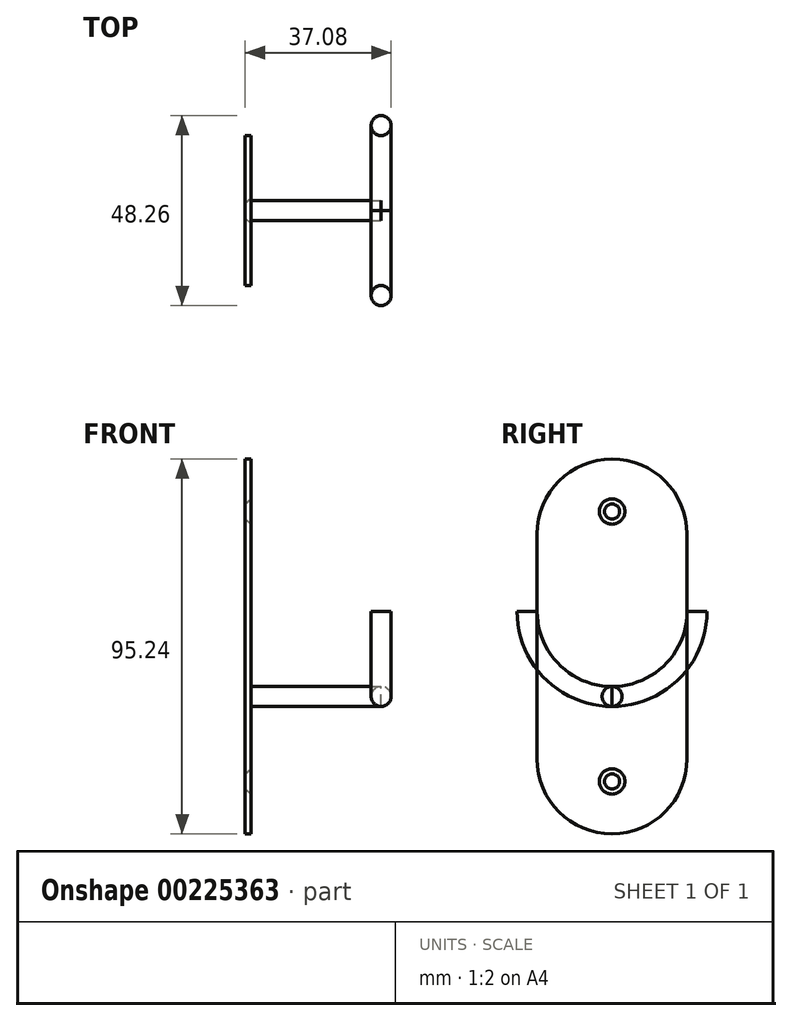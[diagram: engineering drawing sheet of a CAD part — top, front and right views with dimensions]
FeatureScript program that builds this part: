
annotation { "Feature Type Name" : "Feature", "Feature Type Description" : "" }
export const myFeature = defineFeature(function(context is Context, id is Id, definition is map)
    precondition{}
    {
        {
            var Q0;
            Q0=qCreatedBy(makeId("Right.planeOp"),FACE);
            var sketch = newSketch(context, id + "F0", { "sketchPlane" : qUnion([Q0])});
            skCircle(sketch, "E0", {"center": v(0, 0) * mm, "radius": 19.05 * mm, "construction": true});
            skLineSegment(sketch, "E1", {"start": v(-19.05, 0) * mm, "end": v(-19.05, 28.58) * mm});
            skArc(sketch, "E2", {"start": v(0, 47.63) * mm, "mid": v(-13.47, 42.05) * mm, "end": v(-19.05, 28.58) * mm});
            skLineSegment(sketch, "E3", {"start": v(0, 47.62) * mm, "end": v(0, 0) * mm, "construction": true});
            skArc(sketch, "E4.MirrorCS", {"start": v(0, 47.63) * mm, "mid": v(13.47, 42.05) * mm, "end": v(19.05, 28.58) * mm});
            skLineSegment(sketch, "E5.MirrorCS", {"start": v(19.05, 0) * mm, "end": v(19.05, 28.58) * mm});
            skLineSegment(sketch, "E6.MirrorCS", {"start": v(19.05, 0) * mm, "end": v(19.05, -28.58) * mm});
            skLineSegment(sketch, "E7.MirrorCS", {"start": v(-19.05, 0) * mm, "end": v(-19.05, -28.58) * mm});
            skArc(sketch, "E8.MirrorCS", {"start": v(0, -47.63) * mm, "mid": v(-13.47, -42.05) * mm, "end": v(-19.05, -28.58) * mm});
            skArc(sketch, "E9.MirrorCS", {"start": v(0, -47.63) * mm, "mid": v(13.47, -42.05) * mm, "end": v(19.05, -28.58) * mm});
            skSolve(sketch);
        }
        {
            var Q0;
            Q0 = qSketchRegion(id + "F0", true);
            extrude(context, id + "F1", {"entities" : qUnion([Q0]), "depth" : 1.52 * mm});
        }
        {
            var Q0;
            Q0=makeQuery(id+"F1.opExtrude","CAP_FACE",FACE,{"disambiguationData":[OSD([sQuery(id+"F0.wireOp",EDGE,"E1"),sQuery(id+"F0.wireOp",EDGE,"E2"),sQuery(id+"F0.wireOp",EDGE,"E4.MirrorCS"),sQuery(id+"F0.wireOp",EDGE,"E5.MirrorCS"),sQuery(id+"F0.wireOp",EDGE,"E6.MirrorCS"),sQuery(id+"F0.wireOp",EDGE,"E7.MirrorCS"),sQuery(id+"F0.wireOp",EDGE,"E8.MirrorCS"),sQuery(id+"F0.wireOp",EDGE,"E9.MirrorCS")])],"isStart":false});
            var sketch = newSketch(context, id + "F2", { "sketchPlane" : qUnion([Q0])});
            skCircle(sketch, "E10", {"center": v(0, -12.7) * mm, "radius": 2.54 * mm});
            skSolve(sketch);
        }
        {
            var Q0;
            Q0=qCreatedBy(makeId("Front.planeOp"),FACE);
            var sketch = newSketch(context, id + "F3", { "sketchPlane" : qUnion([Q0])});
            skLineSegment(sketch, "E11", {"start": v(1.52, -12.7) * mm, "end": v(34.54, -12.7) * mm});
            skPoint(sketch, "E12.visualSharp", {"position": v(39.62, 0) * mm});
            skSolve(sketch);
        }
        {
            var Q0;
            Q0=makeQuery(id+"F2.imprint","IMPRINT",FACE,{"disambiguationData":[TD([[makeQuery(id+"F2.imprint","IMPRINT",EDGE,{"derivedFrom":sQuery(id+"F2.wireOp",EDGE,"E10")}),1.0]])]});
            var Q1;
            Q1=sQuery(id+"F3.wireOp",EDGE,"E11");
            var Q2;
            Q2=sQuery(id+"F3.wireOp",EDGE,"E12.filletArc");
            var Q3;
            Q3=sQuery(id+"F3.wireOp",EDGE,"HbS3xrMF-i96V-7IMf-6L1r-U0t4GLgRudZ7");
            sweep(context, id + "F4", {"operationType" : NewBodyOperationType.ADD, "profiles" : qUnion([Q0]), "path" : qUnion([Q1, Q2, Q3])});
        }
        {
            var Q0;
            Q0=makeQuery(id+"F2.imprint","IMPRINT",FACE,{"disambiguationData":[TD([[makeQuery(id+"F2.imprint","IMPRINT",EDGE,{"derivedFrom":sQuery(id+"F2.wireOp",EDGE,"E10")}),-1.0]])]});
            var sketch = newSketch(context, id + "F5", { "sketchPlane" : qUnion([Q0])});
            skCircle(sketch, "E13", {"center": v(0, -34.3) * mm, "radius": 2.7 * mm});
            skCircle(sketch, "E14", {"center": v(0, 34.3) * mm, "radius": 2.7 * mm});
            skSolve(sketch);
        }
        {
            var Q0;
            Q0=sQuery(id+"F5.wireOp",VERTEX,"E13.center");
            var Q1;
            Q1=sQuery(id+"F5.wireOp",VERTEX,"E14.center");
            var Q2;
            Q2=makeQuery(id+"F1.opExtrude","SWEPT_BODY",BODY,{"disambiguationData":[OSD([sQuery(id+"F0.wireOp",EDGE,"E0")])]});
            var Q3;
            Q3=makeQuery(id+"F1.opExtrude","SWEPT_BODY",BODY,{"disambiguationData":[OSD([sQuery(id+"F0.wireOp",EDGE,"E1"),sQuery(id+"F0.wireOp",EDGE,"E2"),sQuery(id+"F0.wireOp",EDGE,"E4.MirrorCS"),sQuery(id+"F0.wireOp",EDGE,"E5.MirrorCS"),sQuery(id+"F0.wireOp",EDGE,"E6.MirrorCS"),sQuery(id+"F0.wireOp",EDGE,"E7.MirrorCS"),sQuery(id+"F0.wireOp",EDGE,"E8.MirrorCS"),sQuery(id+"F0.wireOp",EDGE,"E9.MirrorCS")])]});
            hole(context, id + "F6", {"style" : HoleStyle.C_SINK, "endStyle" : HoleEndStyle.THROUGH, "holeDiameter" : 3.26 * mm, "cSinkDiameter" : 6.48 * mm, "cSinkAngle" : 82 * degree, "majorDiameter" : 6.35 * mm, "locations" : qUnion([Q0, Q1]), "scope" : qUnion([Q2, Q3]), "isTappedThrough" : true, "tappedDepth" : 12.7 * mm, "tapClearance" : 3});
        }
        {
            var Q0;
            Q0=qCreatedBy(makeId("Front.planeOp"),FACE);
            var sketch = newSketch(context, id + "F7", { "sketchPlane" : qUnion([Q0])});
            skCircle(sketch, "E15", {"center": v(34.54, -12.7) * mm, "radius": 2.54 * mm});
            skSolve(sketch);
        }
        {
            var Q0;
            Q0=makeQuery(id+"F4.opSweep","CAP_FACE",FACE,{"disambiguationData":[OSD([sQuery(id+"F2.wireOp",EDGE,"E10"),sQuery(id+"F3.wireOp",VERTEX,"E11.end")])],"isStart":false});
            var sketch = newSketch(context, id + "F8", { "sketchPlane" : qUnion([Q0])});
            skArc(sketch, "E16", {"start": v(-21.59, 8.9) * mm, "mid": v(-15.27, -6.38) * mm, "end": v(0, -12.7) * mm});
            skLineSegment(sketch, "E17", {"start": v(0, -12.7) * mm, "end": v(29.58, -12.7) * mm, "construction": true});
            skSolve(sketch);
        }
        {
            var Q0;
            Q0=makeQuery(id+"F7.imprint","IMPRINT",FACE,{"disambiguationData":[TD([[makeQuery(id+"F7.imprint","IMPRINT",EDGE,{"derivedFrom":sQuery(id+"F7.wireOp",EDGE,"E15")}),1.0]])]});
            var Q1;
            Q1=sQuery(id+"F8.wireOp",EDGE,"E16");
            sweep(context, id + "F9", {"profiles" : qUnion([Q0]), "path" : qUnion([Q1])});
        }
        {
            var Q0;
            Q0=makeQuery(id+"F9.opSweep","SWEPT_BODY",BODY,{"disambiguationData":[OSD([sQuery(id+"F7.wireOp",EDGE,"E15"),sQuery(id+"F8.wireOp",EDGE,"E16")])]});
            var Q1;
            Q1=qCreatedBy(makeId("Front.planeOp"),FACE);
            mirror(context, id + "F10", {"entities" : qUnion([Q0]), "mirrorPlane" : qUnion([Q1])});
        }
    });
